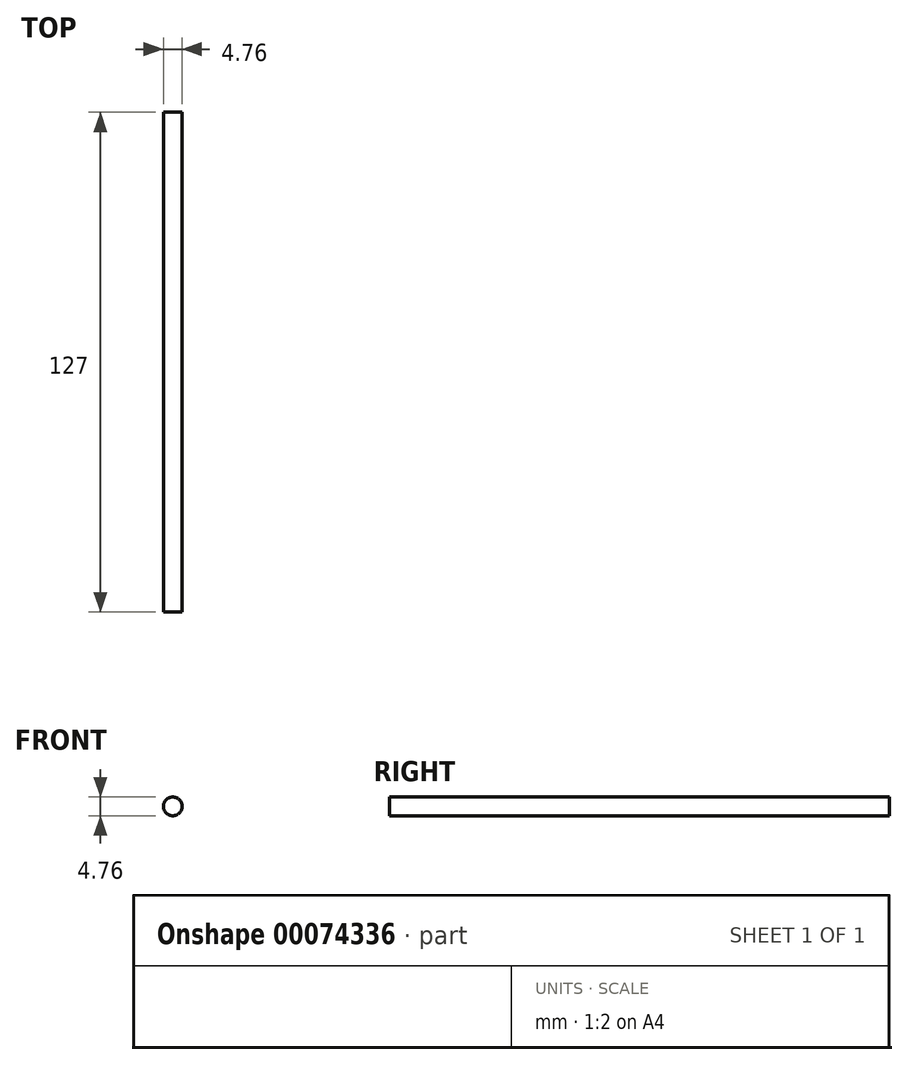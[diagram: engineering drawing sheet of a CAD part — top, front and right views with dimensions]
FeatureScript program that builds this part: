
annotation { "Feature Type Name" : "Feature", "Feature Type Description" : "" }
export const myFeature = defineFeature(function(context is Context, id is Id, definition is map)
    precondition{}
    {
        {
            var Q0;
            Q0=qCreatedBy(makeId("Front.planeOp"),FACE);
            var sketch = newSketch(context, id + "F0", { "sketchPlane" : qUnion([Q0])});
            skCircle(sketch, "E0", {"center": v(0, 0) * mm, "radius": 2.38 * mm});
            skSolve(sketch);
        }
        {
            var Q0;
            Q0=makeQuery(id+"F0.imprint","IMPRINT",FACE,{"disambiguationData":[TD([[makeQuery(id+"F0.imprint","IMPRINT",EDGE,{"derivedFrom":sQuery(id+"F0.wireOp",EDGE,"E0")}),1.0]])]});
            extrude(context, id + "F1", {"entities" : qUnion([Q0]), "depth" : 127 * mm});
        }
    });
